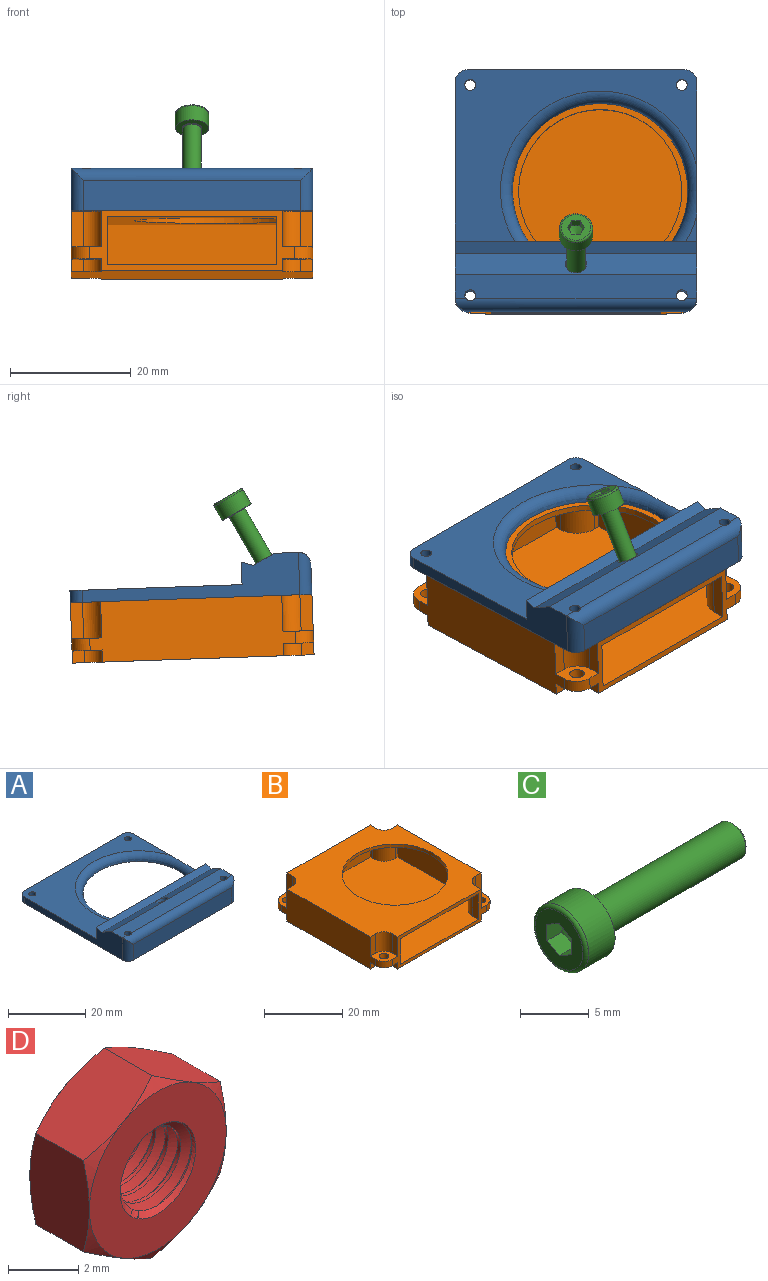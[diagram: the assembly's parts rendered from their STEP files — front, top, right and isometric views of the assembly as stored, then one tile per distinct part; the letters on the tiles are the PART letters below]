
ASSEMBLY  parts=4 mates=1
PART A: 37 faces, bbox 43.4x40x8.4 mm
  f0: plane 40x28.5mm, normal (0,0,1), area 437.1mm2, adj f8,f9,f13,f14,f15,f18,f27,f31
  f1: cylinder r=14.5mm len=5.65mm, axis (0,0,-1), area 14.3mm2, adj f2,f7,f18,f25
  f2: plane 40x40mm, normal (0,0,-1), area 892.9mm2, adj f1,f4,f7,f8,f9,f12,f13,f21
  f3: plane 4.47x1.86mm, normal (0,0,1), area 3.6mm2, adj f8,f18,f27
  f4: plane 5.63x5.51mm, normal (-0.87,0.44,-0.23), area 18.5mm2, adj f2,f5,f21,f23,f24,f25,f26
  f5: plane 3.74x2.3mm, normal (-0.87,-0.44,0.23), area 6.1mm2, adj f4,f6,f24,f25
  f6: plane 3.29x0.96mm, normal (0,-0.88,0.47), area 3.6mm2, adj f5,f7,f24,f25
  f7: plane 4.8x4.3mm, normal (0.87,-0.44,0.23), area 10.5mm2, adj f1,f2,f6,f22,f24,f25
  f8: plane 36x7mm, normal (1,0,0), area 112.8mm2, adj f0,f2,f3,f16,f17,f18,f19,f27
  f9: plane 36x7mm, normal (-1,0,0), area 113mm2, adj f0,f2,f16,f17,f18,f19,f29,f32
  f10: cylinder r=0.9mm len=6.7mm, axis (0,0,-1), area 37.9mm2, adj f19,f30,f34
  f11: cylinder r=0.9mm len=6.7mm, axis (0,0,-1), area 37.9mm2, adj f19,f30,f33
  f12: plane 36x5mm, normal (0,-1,0), area 180mm2, adj f2,f28,f29,f30
  f13: plane 36x2mm, normal (0,1,0), area 72mm2, adj f0,f2,f31,f32
  f14: cylinder r=0.9mm len=1.8mm, axis (0,0,-1), area 9.6mm2, adj f0,f36
  f15: cylinder r=0.9mm len=1.8mm, axis (0,0,-1), area 9.6mm2, adj f0,f35
  f16: plane 40x3.53mm, normal (0,0.47,0.88), area 150.4mm2, adj f8,f9,f17,f19,f20
  f17: plane 40x2mm, normal (0,-0.29,0.96), area 83.7mm2, adj f8,f9,f16,f18
  f18: plane 40x5.73mm, normal (0,1,0), area 151.4mm2, adj f0,f1,f3,f8,f9,f17,f25,f26
  f19: plane 40x3.97mm, normal (0,0,1), area 154.5mm2, adj f8,f9,f10,f11,f16,f30
  f20: cylinder r=1.75mm len=4.03mm, axis (0,0.47,0.88), area 22mm2, adj f16,f24
  f21: plane 1.9x1.05mm, normal (-0.87,-0.44,0.23), area 1.1mm2, adj f2,f4,f26
  f22: plane 5.63x5.51mm, normal (0.87,0.44,-0.23), area 18.5mm2, adj f2,f7,f23,f24
  f23: plane 5.63x3.29mm, normal (0,0.88,-0.47), area 21mm2, adj f2,f4,f22,f24
  f24: plane 6.58x5.03mm, normal (0,-0.47,-0.88), area 18.5mm2, adj f4,f5,f6,f7,f20,f22,f23
  f25: plane 23.49x6mm, normal (0,0,-1), area 86.2mm2, adj f1,f4,f5,f6,f7,f18,f26
  f26: cylinder r=14.5mm len=12.99mm, axis (0,0,-1), area 29.3mm2, adj f2,f4,f18,f21,f25
  f27: torus R=16.5mm, axis (0,0,-1), area 204.3mm2, adj f0,f2,f3,f8,f18
  f28: cylinder r=2mm len=7mm, axis (0,0,1), area 19.7mm2, adj f2,f8,f12,f30
  f29: cylinder r=2mm len=7mm, axis (0,0,-1), area 19.7mm2, adj f2,f9,f12,f30
  f30: cylinder r=2mm len=40mm, axis (-1,0,0), area 120.3mm2, adj f10,f11,f12,f19,f28,f29
  f31: cylinder r=2mm len=2mm, axis (0,0,-1), area 6.3mm2, adj f0,f2,f8,f13
  f32: cylinder r=2mm len=2mm, axis (0,0,1), area 6.3mm2, adj f0,f2,f9,f13
  f33: cone r=1.2mm half-angle=45deg, axis (0,0,-1), area 2.8mm2, adj f2,f11
  f34: cone r=1.2mm half-angle=45deg, axis (0,0,-1), area 2.8mm2, adj f2,f10
  f35: cone r=1.2mm half-angle=45deg, axis (0,0,-1), area 2.8mm2, adj f2,f15
  f36: cone r=1.2mm half-angle=45deg, axis (0,0,-1), area 2.8mm2, adj f2,f14
PART B: 64 faces, bbox 40x40x10 mm
  f0: plane 34x10mm, normal (0,-1,0), area 84mm2, adj f7,f8,f17,f18,f21,f22,f24,f25
  f1: cylinder r=13.5mm len=27mm, axis (0,0,1), area 84.8mm2, adj f22,f59
  f2: plane 6x2mm, normal (-1,0,0), area 12mm2, adj f12,f22,f34,f35
  f3: plane 6x2mm, normal (0,1,0), area 12mm2, adj f15,f22,f34,f35
  f4: plane 6x2mm, normal (0,1,0), area 12mm2, adj f20,f22,f31,f36
  f5: plane 6x2mm, normal (1,0,0), area 12mm2, adj f12,f22,f31,f36
  f6: plane 6x2mm, normal (0,-1,0), area 12mm2, adj f15,f22,f28,f37
  f7: plane 6x2mm, normal (-1,0,0), area 12mm2, adj f0,f22,f28,f37
  f8: plane 6x2mm, normal (1,0,0), area 12mm2, adj f0,f22,f25,f38
  f9: plane 6x2mm, normal (0,-1,0), area 12mm2, adj f20,f22,f25,f38
  f10: plane 2x2mm, normal (0,1,0), area 4mm2, adj f20,f21,f30,f43
  f11: plane 2x2mm, normal (1,0,0), area 4mm2, adj f12,f21,f30,f43
  f12: plane 34x10mm, normal (0,1,0), area 308mm2, adj f2,f5,f11,f13,f21,f22,f30,f31
  f13: plane 2x2mm, normal (-1,0,0), area 4mm2, adj f12,f21,f33,f44
  f14: plane 2x2mm, normal (0,1,0), area 4mm2, adj f15,f21,f33,f44
  f15: plane 34x10mm, normal (-1,0,0), area 308mm2, adj f3,f6,f14,f16,f21,f22,f27,f28
  f16: plane 2x2mm, normal (0,-1,0), area 4mm2, adj f15,f21,f27,f45
  f17: plane 2x2mm, normal (-1,0,0), area 4mm2, adj f0,f21,f27,f45
  f18: plane 2x2mm, normal (1,0,0), area 4mm2, adj f0,f21,f24,f46
  f19: plane 2x2mm, normal (0,-1,0), area 4mm2, adj f20,f21,f24,f46
  f20: plane 34x10mm, normal (1,0,0), area 308mm2, adj f4,f9,f10,f19,f21,f22,f24,f25
  f21: plane 40x40mm, normal (0,0,-1), area 1507.7mm2, adj f0,f10,f11,f12,f13,f14,f15,f16
  f22: plane 40x40mm, normal (0,0,1), area 935.2mm2, adj f0,f1,f2,f3,f4,f5,f6,f7
  f23: cylinder r=1.2mm len=2.4mm, axis (0,0,1), area 15.1mm2, adj f24,f25
  f24: plane 5x5mm, normal (0,0,-1), area 16.6mm2, adj f0,f18,f19,f20,f23,f40,f46
  f25: plane 5x5mm, normal (0,0,1), area 16.6mm2, adj f0,f8,f9,f20,f23,f38,f40
  f26: cylinder r=1.2mm len=2.4mm, axis (0,0,1), area 15.1mm2, adj f27,f28
  f27: plane 5x5mm, normal (0,0,-1), area 16.6mm2, adj f0,f15,f16,f17,f26,f39,f45
  f28: plane 5x5mm, normal (0,0,1), area 16.6mm2, adj f0,f6,f7,f15,f26,f37,f39
  f29: cylinder r=1.2mm len=2.4mm, axis (0,0,1), area 15.1mm2, adj f30,f31
  f30: plane 5x5mm, normal (0,0,-1), area 16.6mm2, adj f10,f11,f12,f20,f29,f41,f43
  f31: plane 5x5mm, normal (0,0,1), area 16.6mm2, adj f4,f5,f12,f20,f29,f36,f41
  f32: cylinder r=1.2mm len=2.4mm, axis (0,0,1), area 15.1mm2, adj f33,f34
  f33: plane 5x5mm, normal (0,0,-1), area 16.6mm2, adj f12,f13,f14,f15,f32,f42,f44
  f34: plane 5x5mm, normal (0,0,1), area 16.6mm2, adj f2,f3,f12,f15,f32,f35,f42
  f35: cylinder r=3mm len=6mm, axis (0,0,-1), area 28.3mm2, adj f2,f3,f22,f34
  f36: cylinder r=3mm len=6mm, axis (0,0,-1), area 28.3mm2, adj f4,f5,f22,f31
  f37: cylinder r=3mm len=6mm, axis (0,0,-1), area 28.3mm2, adj f6,f7,f22,f28
  f38: cylinder r=3mm len=6mm, axis (0,0,-1), area 28.3mm2, adj f8,f9,f22,f25
  f39: cylinder r=3mm len=3mm, axis (0,0,1), area 9.4mm2, adj f0,f15,f27,f28
  f40: cylinder r=3mm len=3mm, axis (0,0,-1), area 9.4mm2, adj f0,f20,f24,f25
  f41: cylinder r=3mm len=3mm, axis (0,0,1), area 9.4mm2, adj f12,f20,f30,f31
  f42: cylinder r=3mm len=3mm, axis (0,0,-1), area 9.4mm2, adj f12,f15,f33,f34
  f43: cylinder r=3mm len=3mm, axis (0,0,-1), area 9.4mm2, adj f10,f11,f21,f30
  f44: cylinder r=3mm len=3mm, axis (0,0,-1), area 9.4mm2, adj f13,f14,f21,f33
  f45: cylinder r=3mm len=3mm, axis (0,0,-1), area 9.4mm2, adj f16,f17,f21,f27
  f46: cylinder r=3mm len=3mm, axis (0,0,-1), area 9.4mm2, adj f18,f19,f21,f24
  f47: plane 8x1mm, normal (0,-1,0), area 8mm2, adj f57,f58,f59,f61
  f48: plane 8x1mm, normal (-1,0,0), area 8mm2, adj f49,f58,f59,f61
  f49: plane 28x8mm, normal (0,-1,0), area 224mm2, adj f48,f50,f58,f59
  f50: plane 8x1mm, normal (1,0,0), area 8mm2, adj f49,f58,f59,f60
  f51: plane 8x1mm, normal (0,-1,0), area 8mm2, adj f52,f58,f59,f60
  f52: plane 28x8mm, normal (1,0,0), area 224mm2, adj f51,f53,f58,f59
  f53: plane 8x1mm, normal (0,1,0), area 8mm2, adj f52,f58,f59,f62
  f54: plane 8x2mm, normal (1,0,0), area 16mm2, adj f0,f58,f59,f62
  f55: plane 8x2mm, normal (-1,0,0), area 16mm2, adj f0,f58,f59,f63
  f56: plane 8x1mm, normal (0,1,0), area 8mm2, adj f57,f58,f59,f63
  f57: plane 28x8mm, normal (-1,0,0), area 224mm2, adj f47,f56,f58,f59
  f58: plane 39x38mm, normal (0,0,1), area 1385.7mm2, adj f0,f47,f48,f49,f50,f51,f52,f53
  f59: plane 39x38mm, normal (0,0,-1), area 813.2mm2, adj f0,f1,f47,f48,f49,f50,f51,f52
  f60: cylinder r=4mm len=8mm, axis (0,0,-1), area 50.3mm2, adj f50,f51,f58,f59
  f61: cylinder r=4mm len=8mm, axis (0,0,-1), area 50.3mm2, adj f47,f48,f58,f59
  f62: cylinder r=4mm len=8mm, axis (0,0,-1), area 50.3mm2, adj f53,f54,f58,f59
  f63: cylinder r=4mm len=8mm, axis (0,0,-1), area 50.3mm2, adj f55,f56,f58,f59
PART C: 15 faces, bbox 18.1x6.1x6.1 mm
  f0: cone r=0.72mm half-angle=60deg, axis (-1,0,0), area 6.3mm2, adj f1,f2,f3,f4,f5,f6
  f1: plane 1.73x1.56mm, normal (0,-1,0), area 2.3mm2, adj f0,f2,f6,f7
  f2: plane 1.67x1.25mm, normal (0,-0.5,-0.87), area 2.3mm2, adj f0,f1,f3,f7
  f3: plane 1.67x1.25mm, normal (0,0.5,-0.87), area 2.3mm2, adj f0,f2,f4,f7
  f4: plane 1.67x1.44mm, normal (0,1,0), area 2.3mm2, adj f0,f3,f5,f7
  f5: plane 1.67x1.25mm, normal (0,0.5,0.87), area 2.3mm2, adj f0,f4,f6,f7
  f6: plane 1.67x1.25mm, normal (0,-0.5,0.87), area 2.3mm2, adj f0,f1,f5,f7
  f7: plane 4.95x4.95mm, normal (-1,0,0), area 13.4mm2, adj f1,f2,f3,f4,f5,f6,f8
  f8: torus R=2.45mm, axis (1,0,0), area 7.8mm2, adj f7,f10
  f9: plane 2.43x2.39mm, normal (1,0,0), area 4.5mm2, adj f11
  f10: cylinder r=2.75mm len=5.5mm, axis (1,0,0), area 46.7mm2, adj f8,f12
  f11: cone r=1.35mm half-angle=45deg, axis (-1,0,0), area 3.7mm2, adj f9,f13
  f12: plane 5.6x5.55mm, normal (1,0,0), area 15.7mm2, adj f10,f14
  f13: cylinder r=1.5mm len=14.59mm, axis (1,0,0), area 137.5mm2, adj f11,f14
  f14: torus R=1.6mm, axis (1,0,0), area 1.5mm2, adj f12,f13
PART D: 26 faces, bbox 6.6x3.1x6.6 mm
  f0: cylinder r=1.25mm len=2.5mm, axis (0,1,0), area 3.6mm2, adj f1,f2,f24,f25
  f1: cone r=1.52mm half-angle=45deg, axis (0,1,0), area 1.9mm2, adj f0,f10,f24,f25
  f2: cone r=1.25mm half-angle=45deg, axis (0,-1,0), area 1.9mm2, adj f0,f9,f24,f25
  f3: plane 3.01x2.67mm, normal (-0.5,0,0.87), area 7.1mm2, adj f4,f8,f12,f16,f20,f21
  f4: plane 3.44x2.66mm, normal (-1,0,0), area 7.1mm2, adj f3,f5,f15,f16,f19,f20
  f5: plane 3.01x2.67mm, normal (-0.5,0,-0.87), area 7.1mm2, adj f4,f6,f14,f15,f18,f19
  f6: plane 3.01x2.67mm, normal (0.5,0,-0.87), area 7.1mm2, adj f5,f7,f13,f14,f17,f18
  f7: plane 3.44x2.66mm, normal (1,0,0), area 7.1mm2, adj f6,f8,f11,f13,f17,f22
  f8: plane 3.01x2.67mm, normal (0.5,0,0.87), area 7.1mm2, adj f3,f7,f11,f12,f21,f22
  f9: plane 5.5x5.5mm, normal (0,-1,0), area 16.5mm2, adj f2,f17,f18,f19,f20,f21,f22,f23
  f10: plane 5.5x5.5mm, normal (0,1,0), area 16.5mm2, adj f1,f11,f12,f13,f14,f15,f16,f23
  f11: cone r=4.33mm half-angle=60deg, axis (0,-1,0), area 0.7mm2, adj f7,f8,f10
  f12: cone r=4.33mm half-angle=60deg, axis (0,-1,0), area 0.7mm2, adj f3,f8,f10
  f13: cone r=4.33mm half-angle=60deg, axis (0,-1,0), area 0.7mm2, adj f6,f7,f10
  f14: cone r=4.33mm half-angle=60deg, axis (0,-1,0), area 0.7mm2, adj f5,f6,f10
  f15: cone r=4.33mm half-angle=60deg, axis (0,-1,0), area 0.7mm2, adj f4,f5,f10
  f16: cone r=4.33mm half-angle=60deg, axis (0,-1,0), area 0.7mm2, adj f3,f4,f10
  f17: cone r=4.33mm half-angle=60deg, axis (0,1,0), area 0.7mm2, adj f6,f7,f9
  f18: cone r=4.33mm half-angle=60deg, axis (0,1,0), area 0.7mm2, adj f5,f6,f9
  f19: cone r=4.33mm half-angle=60deg, axis (0,1,0), area 0.7mm2, adj f4,f5,f9
  f20: cone r=4.33mm half-angle=60deg, axis (0,1,0), area 0.7mm2, adj f3,f4,f9
  f21: cone r=4.33mm half-angle=60deg, axis (0,1,0), area 0.7mm2, adj f3,f8,f9
  f22: cone r=4.33mm half-angle=60deg, axis (0,1,0), area 0.7mm2, adj f7,f8,f9
  f23: cylinder r=1.52mm len=3.04mm, axis (0,-1,0), area 2.8mm2, adj f9,f10,f24,f25
  f24: bspline ~3.51x3.04mm, area 11.6mm2, adj f0,f1,f2,f23
  f25: bspline ~3.51x3.04mm, area 11.7mm2, adj f0,f1,f2,f23
PLACE A rot(axis=(-1,0,0),2deg) t=(0,-0.19,-3.93)mm
PLACE B rot(axis=(-1,0,0),2deg) t=(0,-0.19,-3.93)mm
PLACE C rot(axis=(0.69,-0.19,-0.69),158.9deg) t=(0,-62.9,42.2)mm
PLACE D rot(axis=(-0.65,-0.38,0.65),138.6deg) t=(0,-13.83,-0.21)mm
MATE fastened D.f0 <-> A.f20  axis (0,0.5,0.87) through (0,-13.23,0.83)mm
